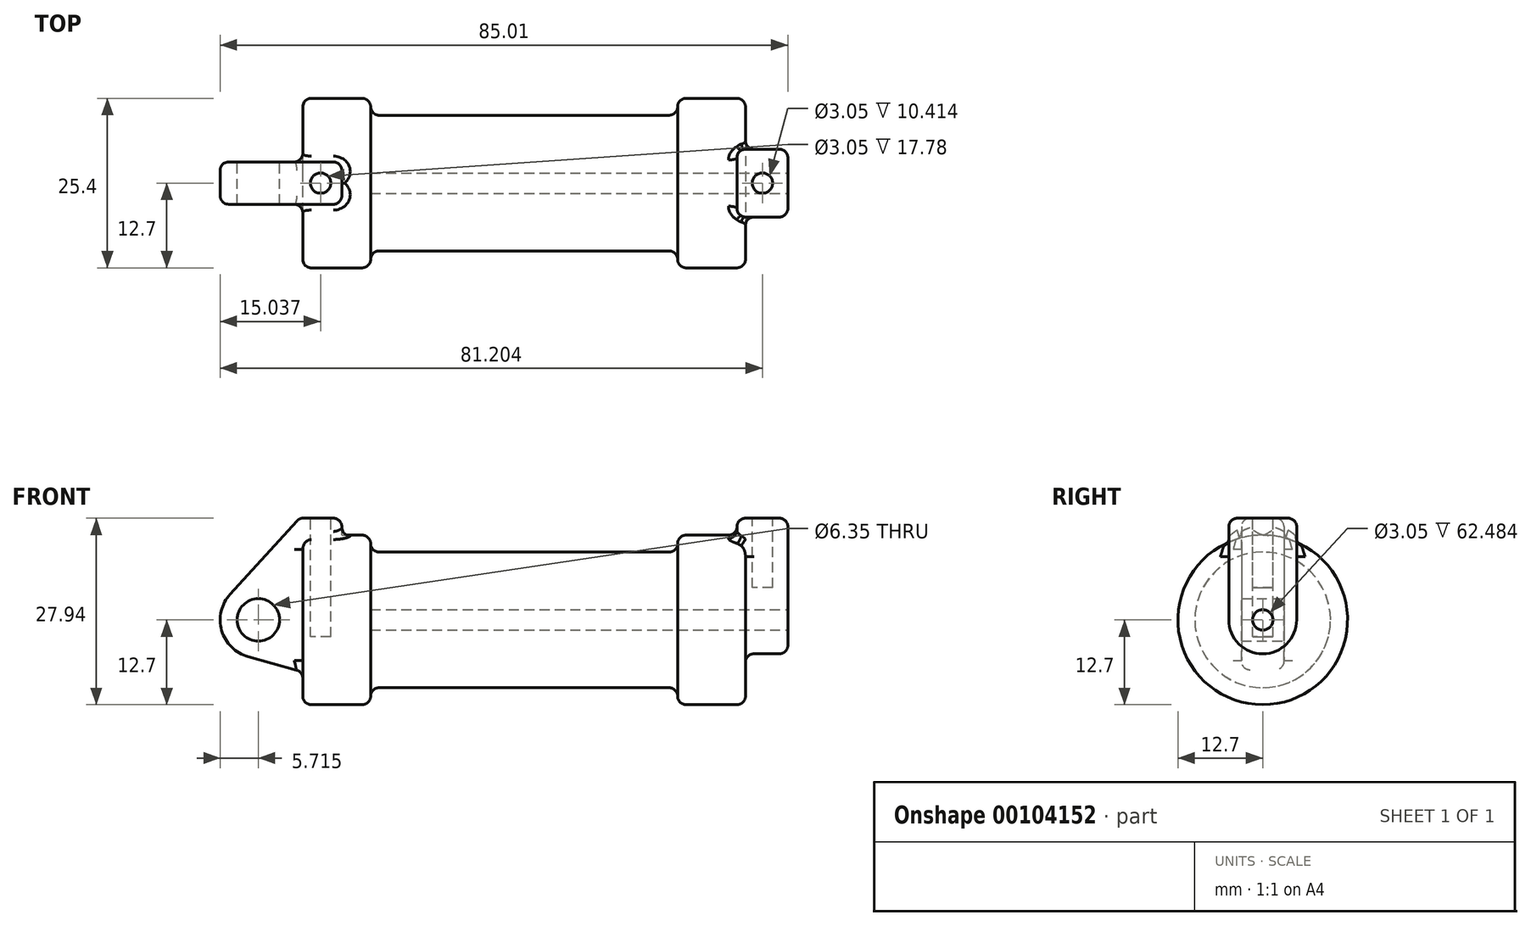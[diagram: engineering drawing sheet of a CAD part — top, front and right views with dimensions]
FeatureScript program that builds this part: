
annotation { "Feature Type Name" : "Feature", "Feature Type Description" : "" }
export const myFeature = defineFeature(function(context is Context, id is Id, definition is map)
    precondition{}
    {
        {
            var Q0;
            Q0=qCreatedBy(makeId("Front.planeOp"),FACE);
            var sketch = newSketch(context, id + "F0", { "sketchPlane" : qUnion([Q0])});
            skLineSegment(sketch, "E0", {"start": v(0, 0) * mm, "end": v(0, 12.7) * mm});
            skLineSegment(sketch, "E1", {"start": v(0, 12.7) * mm, "end": v(10.16, 12.7) * mm});
            skLineSegment(sketch, "E2", {"start": v(10.16, 12.7) * mm, "end": v(10.16, 10.16) * mm});
            skLineSegment(sketch, "E3", {"start": v(10.16, 10.16) * mm, "end": v(56.13, 10.16) * mm});
            skLineSegment(sketch, "E4", {"start": v(56.13, 10.16) * mm, "end": v(56.13, 12.7) * mm});
            skLineSegment(sketch, "E5", {"start": v(56.13, 12.7) * mm, "end": v(66.3, 12.7) * mm});
            skLineSegment(sketch, "E6", {"start": v(66.3, 12.7) * mm, "end": v(66.3, 0) * mm});
            skLineSegment(sketch, "E7", {"start": v(66.3, 0) * mm, "end": v(0, 0) * mm});
            skLineSegment(sketch, "E8", {"start": v(5.84, 15.24) * mm, "end": v(-0.5, 15.24) * mm});
            skLineSegment(sketch, "E9", {"start": v(-0.5, 15.24) * mm, "end": v(-10.88, 3.85) * mm});
            skLineSegment(sketch, "E10", {"start": v(0, 0) * mm, "end": v(-6.65, 0) * mm});
            skCircle(sketch, "E11", {"center": v(-6.65, 0) * mm, "radius": 5.72 * mm});
            skCircle(sketch, "E12", {"center": v(-6.65, 0) * mm, "radius": 3.18 * mm});
            skLineSegment(sketch, "E13", {"start": v(5.84, 15.24) * mm, "end": v(5.84, -9.4) * mm});
            skLineSegment(sketch, "E14", {"start": v(5.84, -9.4) * mm, "end": v(-8.18, -5.5) * mm});
            skSolve(sketch);
        }
        {
            var Q0;
            {var subQ0=sQuery(id+"F0.wireOp",EDGE,"E2");Q0=makeQuery(id+"F0.imprint","IMPRINT",FACE,{"disambiguationData":[TD([[makeQuery(id+"F0.imprint","IMPRINT",EDGE,{"derivedFrom":subQ0}),-1.0]])]});}
            var Q1;
            {var subQ0=sQuery(id+"F0.wireOp",EDGE,"E0");Q1=makeQuery(id+"F0.imprint","IMPRINT",FACE,{"disambiguationData":[TD([[makeQuery(id+"F0.imprint","IMPRINT",EDGE,{"derivedFrom":subQ0}),-1.0]])]});}
            var Q2;
            Q2=sQuery(id+"F0.wireOp",EDGE,"E7");
            revolve(context, id + "F1", {"entities" : qUnion([Q0, Q1]), "axis" : qUnion([Q2]), "revolveType" : RevolveType.FULL});
        }
        {
            var Q0;
            {var subQ0=sQuery(id+"F0.wireOp",EDGE,"E0");Q0=makeQuery(id+"F0.imprint","IMPRINT",FACE,{"disambiguationData":[TD([[makeQuery(id+"F0.imprint","IMPRINT",EDGE,{"derivedFrom":subQ0}),-1.0]])]});}
            var Q1;
            {var subQ3=sQuery(id+"F0.wireOp",EDGE,"E0");Q1=makeQuery(id+"F0.imprint","IMPRINT",FACE,{"disambiguationData":[TD([[makeQuery(id+"F0.imprint","IMPRINT",EDGE,{"derivedFrom":subQ3}),1.0]])]});}
            var Q2;
            {var subQ0=sQuery(id+"F0.wireOp",EDGE,"E14");Q2=makeQuery(id+"F0.imprint","IMPRINT",FACE,{"disambiguationData":[TD([[makeQuery(id+"F0.imprint","IMPRINT",EDGE,{"derivedFrom":subQ0}),-1.0]])]});}
            var Q3;
            {var subQ4=sQuery(id+"F0.wireOp",EDGE,"E12");Q3=makeQuery(id+"F0.imprint","IMPRINT",FACE,{"disambiguationData":[TD([[makeQuery(id+"F0.imprint","IMPRINT",EDGE,{"derivedFrom":subQ4}),-1.0]])]});}
            extrude(context, id + "F2", {"entities" : qUnion([Q0, Q1, Q2, Q3]), "operationType" : NewBodyOperationType.ADD, "endBound" : BoundingType.SYMMETRIC, "depth" : 6.35 * mm});
        }
        {
            var Q0;
            Q0=makeQuery(id+"F1.opRevolve","SWEPT_FACE",FACE,{"disambiguationData":[OSD([sQuery(id+"F0.wireOp",EDGE,"E6")])]});
            var sketch = newSketch(context, id + "F3", { "sketchPlane" : qUnion([Q0])});
            skCircle(sketch, "E15", {"center": v(0, 0) * mm, "radius": 1.52 * mm});
            skCircle(sketch, "E16", {"center": v(0, 0) * mm, "radius": 5.08 * mm});
            skLineSegment(sketch, "E17", {"start": v(-5.08, 0) * mm, "end": v(-5.08, 15.24) * mm});
            skLineSegment(sketch, "E18", {"start": v(5.08, 0) * mm, "end": v(5.08, 15.24) * mm});
            skLineSegment(sketch, "E19", {"start": v(-5.08, 15.24) * mm, "end": v(5.08, 15.24) * mm});
            skSolve(sketch);
        }
        {
            var Q0;
            Q0 = qSketchRegion(id + "F3", true);
            extrude(context, id + "F4", {"entities" : qUnion([Q0]), "operationType" : NewBodyOperationType.ADD, "oppositeDirection" : true, "depth" : 1.27 * mm, "hasSecondDirection" : true, "secondDirectionOppositeDirection" : false, "secondDirectionDepth" : 6.35 * mm});
        }
        {
            var Q0;
            Q0=makeQuery(id+"F4.boolean.opBoolean","SPLIT",FACE,{"disambiguationData":[TD([makeQuery(id+"F4.opExtrude","SWEPT_FACE",FACE,{"disambiguationData":[OSD([sQuery(id+"F3.wireOp",EDGE,"E15")])]})])],"derivedFrom":makeQuery(id+"F1.opRevolve","SWEPT_FACE",FACE,{"disambiguationData":[OSD([sQuery(id+"F0.wireOp",EDGE,"E6")])]})});
            var Q1;
            Q1=makeQuery(id+"F1.opRevolve","SWEPT_FACE",FACE,{"disambiguationData":[OSD([sQuery(id+"F0.wireOp",EDGE,"E2")])]});
            extrude(context, id + "F5", {"entities" : qUnion([Q0]), "operationType" : NewBodyOperationType.REMOVE, "endBound" : BoundingType.UP_TO_SURFACE, "oppositeDirection" : true, "endBoundEntityFace" : qUnion([Q1]), "depth" : 25.4 * mm});
        }
        {
            var Q0;
            Q0=makeQuery(id+"F2.opExtrude","SWEPT_FACE",FACE,{"disambiguationData":[OSD([sQuery(id+"F0.wireOp",EDGE,"E8")])]});
            var sketch = newSketch(context, id + "F6", { "sketchPlane" : qUnion([Q0])});
            skLineSegment(sketch, "E20", {"start": v(2.67, 3.18) * mm, "end": v(2.67, 1.52) * mm});
            skCircle(sketch, "E21", {"center": v(2.67, 0) * mm, "radius": 1.52 * mm});
            skLineSegment(sketch, "E22.trimOffspring", {"start": v(2.67, -1.52) * mm, "end": v(2.67, -3.18) * mm});
            skSolve(sketch);
        }
        {
            var Q0;
            Q0=makeQuery(id+"F4.opExtrude","SWEPT_FACE",FACE,{"disambiguationData":[OSD([sQuery(id+"F3.wireOp",EDGE,"E19")])]});
            var sketch = newSketch(context, id + "F7", { "sketchPlane" : qUnion([Q0])});
            skLineSegment(sketch, "E23", {"start": v(68.83, 5.08) * mm, "end": v(68.83, 1.52) * mm});
            skCircle(sketch, "E24", {"center": v(68.83, 0) * mm, "radius": 1.52 * mm});
            skLineSegment(sketch, "E25.trimOffspring", {"start": v(68.83, -1.52) * mm, "end": v(68.83, -5.08) * mm});
            skSolve(sketch);
        }
        {
            var Q0;
            {var subQ0=sQuery(id+"F7.wireOp",EDGE,"E24");var subQ1=makeQuery(id+"F7.imprint","INTERSECT",VERTEX,{"derivedFrom":[sQuery(id+"F7.wireOp",EDGE,"E23"),subQ0]});Q0=makeQuery(id+"F7.imprint","IMPRINT",FACE,{"disambiguationData":[TD([[makeQuery(id+"F7.imprint","IMPRINT",EDGE,{"disambiguationData":[TD([[subQ1,-1.0]])],"derivedFrom":subQ0}),1.0]])]});}
            extrude(context, id + "F8", {"entities" : qUnion([Q0]), "operationType" : NewBodyOperationType.REMOVE, "oppositeDirection" : true, "depth" : 10.4 * mm});
        }
        {
            var Q0;
            {var subQ0=sQuery(id+"F6.wireOp",EDGE,"E21");var subQ1=makeQuery(id+"F6.imprint","INTERSECT",VERTEX,{"derivedFrom":[sQuery(id+"F6.wireOp",EDGE,"E20"),subQ0]});Q0=makeQuery(id+"F6.imprint","IMPRINT",FACE,{"disambiguationData":[TD([[makeQuery(id+"F6.imprint","IMPRINT",EDGE,{"disambiguationData":[TD([[subQ1,-1.0]])],"derivedFrom":subQ0}),1.0]])]});}
            extrude(context, id + "F9", {"entities" : qUnion([Q0]), "operationType" : NewBodyOperationType.REMOVE, "oppositeDirection" : true, "depth" : 17.78 * mm});
        }
        {
            var Q0;
            Q0=makeQuery(id+"F1.opRevolve","SWEPT_EDGE",EDGE,{"disambiguationData":[OSD([sQuery(id+"F0.wireOp",EDGE,"E0"),sQuery(id+"F0.wireOp",EDGE,"E1")])]});
            var Q1;
            Q1=makeQuery(id+"F1.opRevolve","SWEPT_EDGE",EDGE,{"disambiguationData":[OSD([sQuery(id+"F0.wireOp",EDGE,"E1"),sQuery(id+"F0.wireOp",EDGE,"E2")])]});
            var Q2;
            Q2=makeQuery(id+"F1.opRevolve","SWEPT_EDGE",EDGE,{"disambiguationData":[OSD([sQuery(id+"F0.wireOp",EDGE,"E4"),sQuery(id+"F0.wireOp",EDGE,"E5")])]});
            var Q3;
            Q3=makeQuery(id+"F1.opRevolve","SWEPT_EDGE",EDGE,{"disambiguationData":[OSD([sQuery(id+"F0.wireOp",EDGE,"E5"),sQuery(id+"F0.wireOp",EDGE,"E6")])]});
            var Q4;
            Q4=makeQuery(id+"F1.opRevolve","SWEPT_EDGE",EDGE,{"disambiguationData":[OSD([sQuery(id+"F0.wireOp",EDGE,"E2"),sQuery(id+"F0.wireOp",EDGE,"E3")])]});
            var Q5;
            Q5=makeQuery(id+"F1.opRevolve","SWEPT_EDGE",EDGE,{"disambiguationData":[OSD([sQuery(id+"F0.wireOp",EDGE,"E3"),sQuery(id+"F0.wireOp",EDGE,"E4")])]});
            fillet(context, id + "F10", {"entities" : qUnion([Q0, Q1, Q2, Q3, Q4, Q5]), "radius" : 1.27 * mm, "tangentPropagation" : true, "allowEdgeOverflow" : false});
        }
        {
            var Q0;
            Q0=makeQuery(id+"F4.opExtrude","SWEPT_EDGE",EDGE,{"disambiguationData":[OSD([sQuery(id+"F3.wireOp",EDGE,"E17"),sQuery(id+"F3.wireOp",EDGE,"E19")])]});
            var Q1;
            Q1=makeQuery(id+"F4.opExtrude","CAP_EDGE",EDGE,{"disambiguationData":[OSD([sQuery(id+"F3.wireOp",EDGE,"E19")])],"isStart":false});
            var Q2;
            Q2=makeQuery(id+"F4.opExtrude","SWEPT_EDGE",EDGE,{"disambiguationData":[OSD([sQuery(id+"F3.wireOp",EDGE,"E18"),sQuery(id+"F3.wireOp",EDGE,"E19")])]});
            var Q3;
            Q3=makeQuery(id+"F4.opExtrude","CAP_EDGE",EDGE,{"disambiguationData":[OSD([sQuery(id+"F3.wireOp",EDGE,"E19")])],"isStart":true});
            var Q4;
            Q4=makeQuery(id+"F4.opExtrude","CAP_EDGE",EDGE,{"disambiguationData":[OSD([sQuery(id+"F3.wireOp",EDGE,"E17")])],"isStart":false});
            var Q5;
            Q5=makeQuery(id+"F4.opExtrude","CAP_EDGE",EDGE,{"disambiguationData":[OSD([sQuery(id+"F3.wireOp",EDGE,"E18")])],"isStart":false});
            var Q6;
            Q6=makeQuery(id+"F4.boolean.opBoolean","INTERSECT",EDGE,{"derivedFrom":[makeQuery(id+"F1.opRevolve","SWEPT_FACE",FACE,{"disambiguationData":[OSD([sQuery(id+"F0.wireOp",EDGE,"E5")])]}),makeQuery(id+"F4.opExtrude","CAP_FACE",FACE,{"disambiguationData":[OSD([sQuery(id+"F3.wireOp",EDGE,"E15"),sQuery(id+"F3.wireOp",EDGE,"E16"),sQuery(id+"F3.wireOp",EDGE,"E17"),sQuery(id+"F3.wireOp",EDGE,"E18"),sQuery(id+"F3.wireOp",EDGE,"E19")])],"isStart":false})]});
            var Q7;
            Q7=makeQuery(id+"F4.boolean.opBoolean","INTERSECT",EDGE,{"derivedFrom":[makeQuery(id+"F1.opRevolve","SWEPT_FACE",FACE,{"disambiguationData":[OSD([sQuery(id+"F0.wireOp",EDGE,"E6")])]}),makeQuery(id+"F4.opExtrude","SWEPT_FACE",FACE,{"disambiguationData":[OSD([sQuery(id+"F3.wireOp",EDGE,"E16")])]})]});
            var Q8;
            Q8=makeQuery(id+"F4.opExtrude","CAP_EDGE",EDGE,{"disambiguationData":[OSD([sQuery(id+"F3.wireOp",EDGE,"E17")])],"isStart":true});
            var Q9;
            Q9=makeQuery(id+"F4.opExtrude","CAP_EDGE",EDGE,{"disambiguationData":[OSD([sQuery(id+"F3.wireOp",EDGE,"E16")])],"isStart":true});
            var Q10;
            Q10=makeQuery(id+"F4.opExtrude","CAP_EDGE",EDGE,{"disambiguationData":[OSD([sQuery(id+"F3.wireOp",EDGE,"E18")])],"isStart":true});
            var Q11;
            Q11=makeQuery(id+"F4.boolean.opBoolean","INTERSECT",EDGE,{"derivedFrom":[makeQuery(id+"F1.opRevolve","SWEPT_FACE",FACE,{"disambiguationData":[OSD([sQuery(id+"F0.wireOp",EDGE,"E6")])]}),makeQuery(id+"F4.opExtrude","SWEPT_FACE",FACE,{"disambiguationData":[OSD([sQuery(id+"F3.wireOp",EDGE,"E17")])]})]});
            fillet(context, id + "F11", {"entities" : qUnion([Q0, Q1, Q2, Q3, Q4, Q5, Q6, Q7, Q8, Q9, Q10, Q11]), "radius" : 1.27 * mm, "tangentPropagation" : true, "allowEdgeOverflow" : false});
        }
        {
            var Q0;
            Q0=makeQuery(id+"F2.opExtrude","CAP_EDGE",EDGE,{"disambiguationData":[OSD([sQuery(id+"F0.wireOp",EDGE,"E9")])],"isStart":false});
            var Q1;
            Q1=makeQuery(id+"F2.opExtrude","CAP_EDGE",EDGE,{"disambiguationData":[OSD([sQuery(id+"F0.wireOp",EDGE,"E9")])],"isStart":true});
            var Q2;
            Q2=makeQuery(id+"F2.opExtrude","CAP_EDGE",EDGE,{"disambiguationData":[OSD([sQuery(id+"F0.wireOp",EDGE,"E11")])],"isStart":false});
            var Q3;
            Q3=makeQuery(id+"F2.opExtrude","CAP_EDGE",EDGE,{"disambiguationData":[OSD([sQuery(id+"F0.wireOp",EDGE,"E11")])],"isStart":true});
            var Q4;
            Q4=makeQuery(id+"F2.opExtrude","SWEPT_EDGE",EDGE,{"disambiguationData":[OSD([sQuery(id+"F0.wireOp",EDGE,"E11"),sQuery(id+"F0.wireOp",EDGE,"E14")])]});
            var Q5;
            Q5=makeQuery(id+"F2.opExtrude","SWEPT_EDGE",EDGE,{"disambiguationData":[OSD([sQuery(id+"F0.wireOp",EDGE,"E8"),sQuery(id+"F0.wireOp",EDGE,"E9")])]});
            var Q6;
            Q6=makeQuery(id+"F2.opExtrude","CAP_EDGE",EDGE,{"disambiguationData":[OSD([sQuery(id+"F0.wireOp",EDGE,"E14")])],"isStart":true});
            var Q7;
            Q7=makeQuery(id+"F2.boolean.opBoolean","INTERSECT",EDGE,{"derivedFrom":[makeQuery(id+"F1.opRevolve","SWEPT_FACE",FACE,{"disambiguationData":[OSD([sQuery(id+"F0.wireOp",EDGE,"E0")])]}),makeQuery(id+"F2.opExtrude","CAP_FACE",FACE,{"disambiguationData":[OSD([sQuery(id+"F0.wireOp",EDGE,"E8"),sQuery(id+"F0.wireOp",EDGE,"E9"),sQuery(id+"F0.wireOp",EDGE,"E11"),sQuery(id+"F0.wireOp",EDGE,"E12"),sQuery(id+"F0.wireOp",EDGE,"E13"),sQuery(id+"F0.wireOp",EDGE,"E14")])],"isStart":true})]});
            var Q8;
            Q8=makeQuery(id+"F2.opExtrude","CAP_EDGE",EDGE,{"disambiguationData":[OSD([sQuery(id+"F0.wireOp",EDGE,"E14")])],"isStart":false});
            var Q9;
            Q9=makeQuery(id+"F2.boolean.opBoolean","INTERSECT",EDGE,{"derivedFrom":[makeQuery(id+"F1.opRevolve","SWEPT_FACE",FACE,{"disambiguationData":[OSD([sQuery(id+"F0.wireOp",EDGE,"E0")])]}),makeQuery(id+"F2.opExtrude","SWEPT_FACE",FACE,{"disambiguationData":[OSD([sQuery(id+"F0.wireOp",EDGE,"E14")])]})]});
            var Q10;
            Q10=makeQuery(id+"F2.opExtrude","CAP_EDGE",EDGE,{"disambiguationData":[OSD([sQuery(id+"F0.wireOp",EDGE,"E8")])],"isStart":true});
            var Q11;
            Q11=makeQuery(id+"F2.opExtrude","CAP_EDGE",EDGE,{"disambiguationData":[OSD([sQuery(id+"F0.wireOp",EDGE,"E13")])],"isStart":true});
            var Q12;
            Q12=makeQuery(id+"F2.opExtrude","CAP_EDGE",EDGE,{"disambiguationData":[OSD([sQuery(id+"F0.wireOp",EDGE,"E8")])],"isStart":false});
            var Q13;
            Q13=makeQuery(id+"F2.opExtrude","CAP_EDGE",EDGE,{"disambiguationData":[OSD([sQuery(id+"F0.wireOp",EDGE,"E13")])],"isStart":false});
            var Q14;
            Q14=makeQuery(id+"F2.boolean.opBoolean","INTERSECT",EDGE,{"derivedFrom":[makeQuery(id+"F1.opRevolve","SWEPT_FACE",FACE,{"disambiguationData":[OSD([sQuery(id+"F0.wireOp",EDGE,"E0")])]}),makeQuery(id+"F2.opExtrude","CAP_FACE",FACE,{"disambiguationData":[OSD([sQuery(id+"F0.wireOp",EDGE,"E8"),sQuery(id+"F0.wireOp",EDGE,"E9"),sQuery(id+"F0.wireOp",EDGE,"E11"),sQuery(id+"F0.wireOp",EDGE,"E12"),sQuery(id+"F0.wireOp",EDGE,"E13"),sQuery(id+"F0.wireOp",EDGE,"E14")])],"isStart":false})]});
            var Q15;
            Q15=makeQuery(id+"F2.opExtrude","SWEPT_EDGE",EDGE,{"disambiguationData":[OSD([sQuery(id+"F0.wireOp",EDGE,"E8"),sQuery(id+"F0.wireOp",EDGE,"E13")])]});
            fillet(context, id + "F12", {"entities" : qUnion([Q0, Q1, Q2, Q3, Q4, Q5, Q6, Q7, Q8, Q9, Q10, Q11, Q12, Q13, Q14, Q15]), "radius" : 1.27 * mm, "tangentPropagation" : true, "allowEdgeOverflow" : false});
        }
    });
